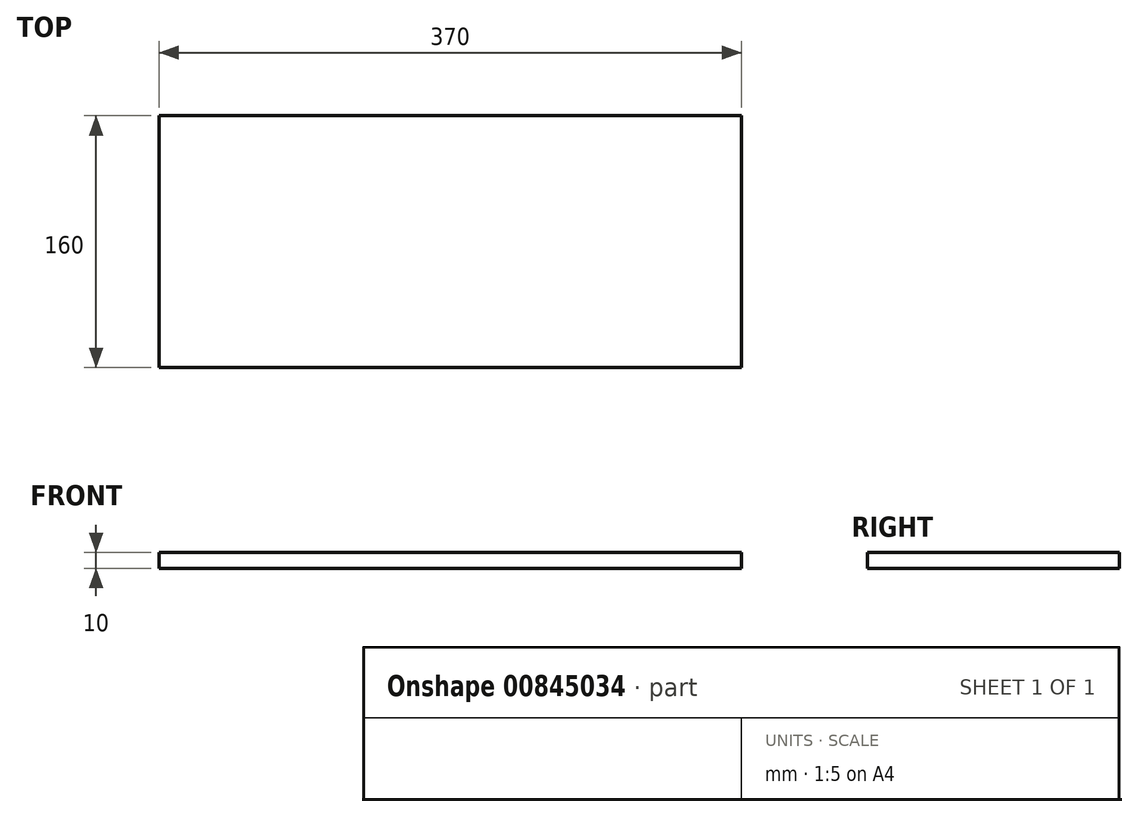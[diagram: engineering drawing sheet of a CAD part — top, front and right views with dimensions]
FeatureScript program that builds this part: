
annotation { "Feature Type Name" : "Feature", "Feature Type Description" : "" }
export const myFeature = defineFeature(function(context is Context, id is Id, definition is map)
    precondition{}
    {
        {
            var Q0;
            Q0=qCreatedBy(makeId("Top.planeOp"),FACE);
            var sketch = newSketch(context, id + "F0", { "sketchPlane" : qUnion([Q0])});
            skLineSegment(sketch, "E0.bottom", {"start": v(-185, 80) * mm, "end": v(185, 80) * mm});
            skLineSegment(sketch, "E0.top", {"start": v(-185, -80) * mm, "end": v(185, -80) * mm});
            skLineSegment(sketch, "E0.left", {"start": v(-185, 80) * mm, "end": v(-185, -80) * mm});
            skLineSegment(sketch, "E0.right", {"start": v(185, 80) * mm, "end": v(185, -80) * mm});
            skPoint(sketch, "E0.middle", {"position": v(0, 0) * mm});
            skSolve(sketch);
        }
        {
            var Q0;
            Q0=makeQuery(id+"F0.imprint","IMPRINT",FACE,{"disambiguationData":[TD([[makeQuery(id+"F0.imprint","IMPRINT",EDGE,{"derivedFrom":sQuery(id+"F0.wireOp",EDGE,"E0.bottom")}),-1.0]])]});
            extrude(context, id + "F1", {"entities" : qUnion([Q0]), "depth" : 10 * mm, "offsetDistance" : 25 * mm});
        }
    });
